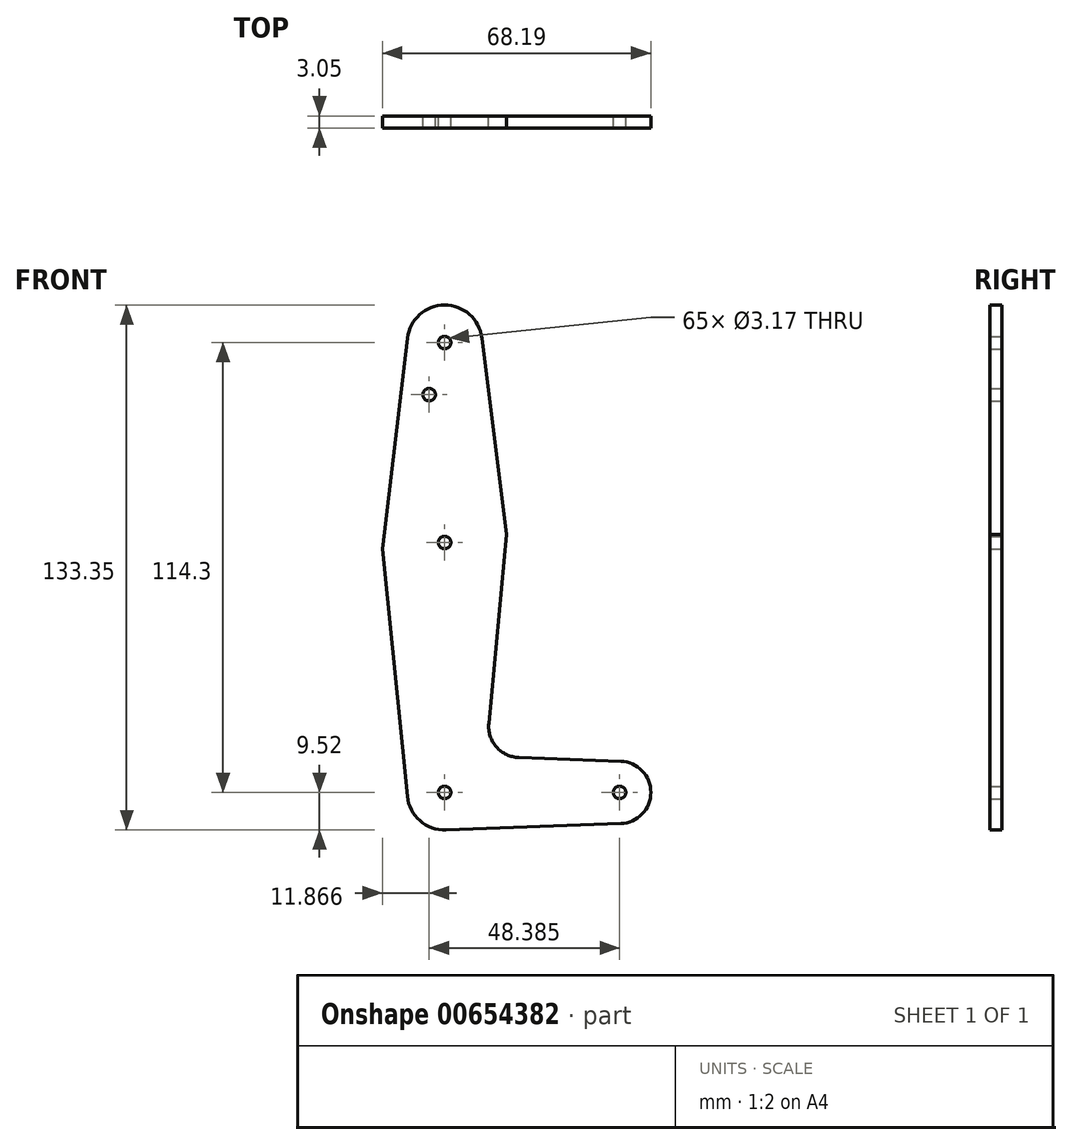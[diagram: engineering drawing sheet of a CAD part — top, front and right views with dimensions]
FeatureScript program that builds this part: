
annotation { "Feature Type Name" : "Feature", "Feature Type Description" : "" }
export const myFeature = defineFeature(function(context is Context, id is Id, definition is map)
    precondition{}
    {
        {
            var Q0;
            Q0=qCreatedBy(makeId("Front.planeOp"),FACE);
            var sketch = newSketch(context, id + "F0", { "sketchPlane" : qUnion([Q0])});
            skLineSegment(sketch, "E0", {"start": v(0, 0) * mm, "end": v(0, 114.3) * mm, "construction": true});
            skLineSegment(sketch, "E1", {"start": v(0, 0) * mm, "end": v(44.45, 0) * mm, "construction": true});
            skCircle(sketch, "E2", {"center": v(0, 114.3) * mm, "radius": 9.53 * mm});
            skCircle(sketch, "E3", {"center": v(0, 63.5) * mm, "radius": 15.88 * mm});
            skCircle(sketch, "E4", {"center": v(0, 0) * mm, "radius": 9.53 * mm});
            skCircle(sketch, "E5", {"center": v(44.45, 0) * mm, "radius": 7.94 * mm});
            skLineSegment(sketch, "E6", {"start": v(9.45, 115.5) * mm, "end": v(15.75, 65.48) * mm});
            skLineSegment(sketch, "E7", {"start": v(15.75, 65.48) * mm, "end": v(11.22, 17.55) * mm});
            skLineSegment(sketch, "E8", {"start": v(18.86, 8.86) * mm, "end": v(44.73, 7.93) * mm});
            skLineSegment(sketch, "E9", {"start": v(0.34, -9.52) * mm, "end": v(44.73, -7.93) * mm});
            skLineSegment(sketch, "E10", {"start": v(-9.48, -0.95) * mm, "end": v(-15.8, 61.91) * mm});
            skLineSegment(sketch, "E11", {"start": v(-15.8, 61.91) * mm, "end": v(-9.46, 115.42) * mm});
            skCircle(sketch, "E12", {"center": v(0, 114.3) * mm, "radius": 1.59 * mm});
            skCircle(sketch, "E13", {"center": v(0, 63.5) * mm, "radius": 1.59 * mm});
            skCircle(sketch, "E14", {"center": v(0, 0) * mm, "radius": 1.59 * mm});
            skCircle(sketch, "E15", {"center": v(44.45, 0) * mm, "radius": 1.59 * mm});
            skArc(sketch, "E16.filletArc", {"start": v(11.22, 17.55) * mm, "mid": v(13.16, 11.56) * mm, "end": v(18.86, 8.86) * mm});
            skCircle(sketch, "E17", {"center": v(-3.93, 101.06) * mm, "radius": 1.59 * mm});
            skSolve(sketch);
        }
        {
            var Q0;
            Q0=makeQuery(id+"F0.imprint","IMPRINT",FACE,{"disambiguationData":[TD([[makeQuery(id+"F0.imprint","IMPRINT",EDGE,{"derivedFrom":sQuery(id+"F0.wireOp",EDGE,"E14")}),-1.0]])]});
            var Q1;
            {var subQ0=sQuery(id+"F0.wireOp",EDGE,"E6");Q1=makeQuery(id+"F0.imprint","IMPRINT",FACE,{"disambiguationData":[TD([[makeQuery(id+"F0.imprint","IMPRINT",EDGE,{"derivedFrom":subQ0}),-1.0]])]});}
            var Q2;
            Q2=makeQuery(id+"F0.imprint","IMPRINT",FACE,{"disambiguationData":[TD([[makeQuery(id+"F0.imprint","IMPRINT",EDGE,{"derivedFrom":sQuery(id+"F0.wireOp",EDGE,"E13")}),-1.0]])]});
            var Q3;
            {var subQ0=sQuery(id+"F0.wireOp",EDGE,"E8");Q3=makeQuery(id+"F0.imprint","IMPRINT",FACE,{"disambiguationData":[TD([[makeQuery(id+"F0.imprint","IMPRINT",EDGE,{"derivedFrom":subQ0}),-1.0]])]});}
            var Q4;
            Q4=makeQuery(id+"F0.imprint","IMPRINT",FACE,{"disambiguationData":[TD([[makeQuery(id+"F0.imprint","IMPRINT",EDGE,{"derivedFrom":sQuery(id+"F0.wireOp",EDGE,"E15")}),-1.0]])]});
            var Q5;
            Q5=makeQuery(id+"F0.imprint","IMPRINT",FACE,{"disambiguationData":[TD([[makeQuery(id+"F0.imprint","IMPRINT",EDGE,{"derivedFrom":sQuery(id+"F0.wireOp",EDGE,"E12")}),-1.0]])]});
            extrude(context, id + "F1", {"entities" : qUnion([Q0, Q1, Q2, Q3, Q4, Q5]), "depth" : 3.05 * mm, "offsetDistance" : 25.4 * mm});
        }
    });
